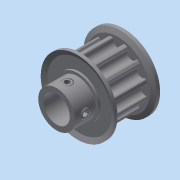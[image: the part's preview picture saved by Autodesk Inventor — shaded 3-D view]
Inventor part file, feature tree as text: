
AUTODESK INVENTOR PART (.ipt)
format: ipt  version: 2015 (Build 190159000, 159)  size: 278,528 bytes
history: native  units: in
note: dims shown in document units (in); Inventor stores cm internally (conversion verified against a paired STEP export)
features: other x1, extrude x1, imported_body x1, sketch x1
ambient origin geometry x8: Origin, YZ Plane, XZ Plane, XY Plane, X Axis, Y Axis, Z Axis, Center Point
bodies: Solid1 (feature_tree)
feature tree (4):
  other  "a_6a25m012df09061"
  extrude  "Extrusion1"  Depth=0.3937in TaperAngle=0.0deg
  imported_body  "Base1"
  sketch  "Sketch1"  dims[d0=0.315in d1=0.3937in d2=0.0in]
